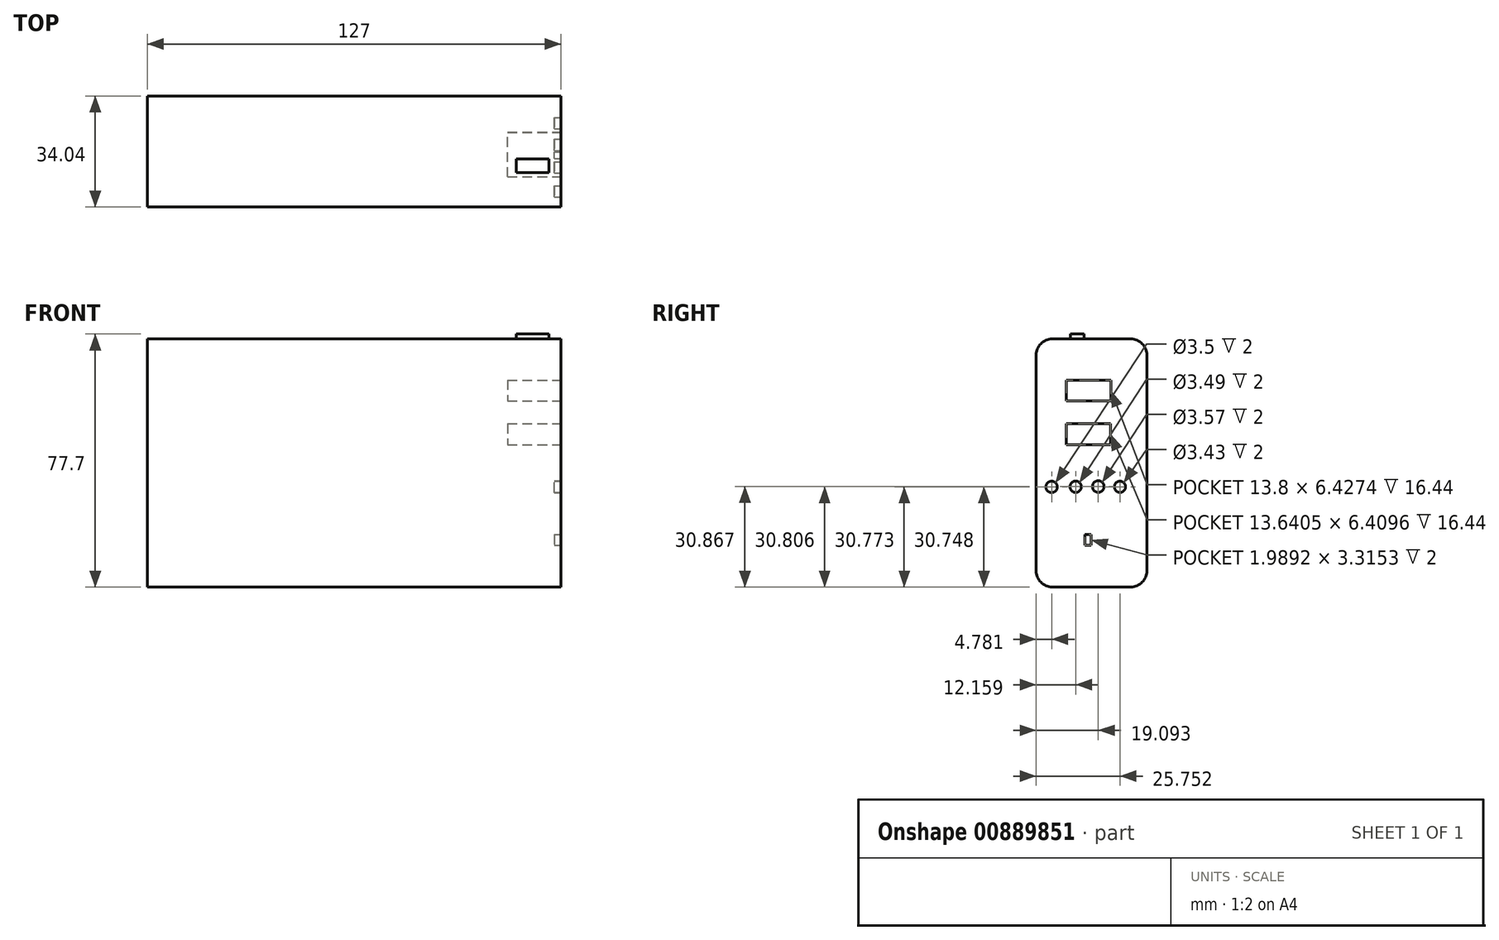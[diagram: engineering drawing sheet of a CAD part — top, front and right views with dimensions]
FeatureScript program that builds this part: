
annotation { "Feature Type Name" : "Feature", "Feature Type Description" : "" }
export const myFeature = defineFeature(function(context is Context, id is Id, definition is map)
    precondition{}
    {
        {
            var Q0;
            Q0=qCreatedBy(makeId("Front.planeOp"),FACE);
            var sketch = newSketch(context, id + "F0", { "sketchPlane" : qUnion([Q0])});
            skLineSegment(sketch, "E0.bottom", {"start": v(63.5, -38.1) * mm, "end": v(-63.5, -38.1) * mm});
            skLineSegment(sketch, "E0.top", {"start": v(63.5, 38.1) * mm, "end": v(-63.5, 38.1) * mm});
            skLineSegment(sketch, "E0.left", {"start": v(63.5, -38.1) * mm, "end": v(63.5, 38.1) * mm});
            skLineSegment(sketch, "E0.right", {"start": v(-63.5, -38.1) * mm, "end": v(-63.5, 38.1) * mm});
            skPoint(sketch, "E0.middle", {"position": v(0, 0) * mm});
            skSolve(sketch);
        }
        {
            var Q0;
            Q0=makeQuery(id+"F0.imprint","IMPRINT",FACE,{"disambiguationData":[TD([[makeQuery(id+"F0.imprint","IMPRINT",EDGE,{"derivedFrom":sQuery(id+"F0.wireOp",EDGE,"E0.bottom")}),-1.0]])]});
            extrude(context, id + "F1", {"entities" : qUnion([Q0]), "depth" : 34.04 * mm, "offsetDistance" : 25.4 * mm});
        }
        {
            var Q0;
            Q0=makeQuery(id+"F1.opExtrude","CAP_EDGE",EDGE,{"disambiguationData":[OSD([sQuery(id+"F0.wireOp",EDGE,"E0.top")])],"isStart":false});
            var Q1;
            Q1=makeQuery(id+"F1.opExtrude","CAP_EDGE",EDGE,{"disambiguationData":[OSD([sQuery(id+"F0.wireOp",EDGE,"E0.top")])],"isStart":true});
            var Q2;
            Q2=makeQuery(id+"F1.opExtrude","CAP_EDGE",EDGE,{"disambiguationData":[OSD([sQuery(id+"F0.wireOp",EDGE,"E0.bottom")])],"isStart":false});
            var Q3;
            Q3=makeQuery(id+"F1.opExtrude","CAP_EDGE",EDGE,{"disambiguationData":[OSD([sQuery(id+"F0.wireOp",EDGE,"E0.bottom")])],"isStart":true});
            fillet(context, id + "F2", {"entities" : qUnion([Q0, Q1, Q2, Q3]), "radius" : 5 * mm, "tangentPropagation" : true, "allowEdgeOverflow" : false});
        }
        {
            var Q0;
            Q0=makeQuery(id+"F1.opExtrude","SWEPT_FACE",FACE,{"disambiguationData":[OSD([sQuery(id+"F0.wireOp",EDGE,"E0.left")])]});
            var sketch = newSketch(context, id + "F3", { "sketchPlane" : qUnion([Q0])});
            skLineSegment(sketch, "E1.bottom", {"start": v(-24.8, 25.43) * mm, "end": v(-11, 25.43) * mm});
            skLineSegment(sketch, "E1.top", {"start": v(-24.8, 19) * mm, "end": v(-11, 19) * mm});
            skLineSegment(sketch, "E1.left", {"start": v(-24.8, 25.43) * mm, "end": v(-24.8, 19) * mm});
            skLineSegment(sketch, "E1.right", {"start": v(-11, 25.43) * mm, "end": v(-11, 19) * mm});
            skSolve(sketch);
        }
        {
            var Q0;
            Q0 = qSketchRegion(id + "F3", true);
            extrude(context, id + "F4", {"entities" : qUnion([Q0]), "operationType" : NewBodyOperationType.REMOVE, "oppositeDirection" : true, "depth" : 16.44 * mm, "offsetDistance" : 25.4 * mm});
        }
        {
            var Q0;
            Q0=makeQuery(id+"F1.opExtrude","SWEPT_FACE",FACE,{"disambiguationData":[OSD([sQuery(id+"F0.wireOp",EDGE,"E0.left")])]});
            var sketch = newSketch(context, id + "F5", { "sketchPlane" : qUnion([Q0])});
            skLineSegment(sketch, "E2.bottom", {"start": v(-24.8, 12.05) * mm, "end": v(-11.16, 12.05) * mm});
            skLineSegment(sketch, "E2.top", {"start": v(-24.8, 5.64) * mm, "end": v(-11.16, 5.64) * mm});
            skLineSegment(sketch, "E2.left", {"start": v(-24.8, 12.05) * mm, "end": v(-24.8, 5.64) * mm});
            skLineSegment(sketch, "E2.right", {"start": v(-11.16, 12.05) * mm, "end": v(-11.16, 5.64) * mm});
            skSolve(sketch);
        }
        {
            var Q0;
            Q0 = qSketchRegion(id + "F5", true);
            extrude(context, id + "F6", {"entities" : qUnion([Q0]), "operationType" : NewBodyOperationType.REMOVE, "oppositeDirection" : true, "depth" : 16.44 * mm, "offsetDistance" : 25.4 * mm});
        }
        {
            var Q0;
            Q0=makeQuery(id+"F1.opExtrude","SWEPT_FACE",FACE,{"disambiguationData":[OSD([sQuery(id+"F0.wireOp",EDGE,"E0.left")])]});
            var sketch = newSketch(context, id + "F7", { "sketchPlane" : qUnion([Q0])});
            skCircle(sketch, "E3", {"center": v(-29.26, -7.35) * mm, "radius": 1.75 * mm});
            skPoint(sketch, "E3.first.point", {"position": v(-30.17, -5.86) * mm});
            skPoint(sketch, "E3.second.point", {"position": v(-28.18, -8.73) * mm});
            skPoint(sketch, "E3.third.point", {"position": v(-27.52, -7.18) * mm});
            skSolve(sketch);
        }
        {
            var Q0;
            Q0 = qSketchRegion(id + "F7", true);
            extrude(context, id + "F8", {"entities" : qUnion([Q0]), "operationType" : NewBodyOperationType.REMOVE, "oppositeDirection" : true, "depth" : 2 * mm, "offsetDistance" : 25.4 * mm});
        }
        {
            var Q0;
            Q0=makeQuery(id+"F1.opExtrude","SWEPT_FACE",FACE,{"disambiguationData":[OSD([sQuery(id+"F0.wireOp",EDGE,"E0.left")])]});
            var sketch = newSketch(context, id + "F9", { "sketchPlane" : qUnion([Q0])});
            skCircle(sketch, "E4", {"center": v(-21.88, -7.3) * mm, "radius": 1.75 * mm});
            skPoint(sketch, "E4.first.point", {"position": v(-23.32, -6.3) * mm});
            skPoint(sketch, "E4.second.point", {"position": v(-20.22, -7.85) * mm});
            skPoint(sketch, "E4.third.point", {"position": v(-20.44, -8.29) * mm});
            skSolve(sketch);
        }
        {
            var Q0;
            Q0 = qSketchRegion(id + "F9", true);
            extrude(context, id + "F10", {"entities" : qUnion([Q0]), "operationType" : NewBodyOperationType.REMOVE, "oppositeDirection" : true, "depth" : 2 * mm, "offsetDistance" : 25.4 * mm});
        }
        {
            var Q0;
            Q0=makeQuery(id+"F1.opExtrude","SWEPT_FACE",FACE,{"disambiguationData":[OSD([sQuery(id+"F0.wireOp",EDGE,"E0.left")])]});
            var sketch = newSketch(context, id + "F11", { "sketchPlane" : qUnion([Q0])});
            skCircle(sketch, "E5", {"center": v(-14.95, -7.23) * mm, "radius": 1.78 * mm});
            skPoint(sketch, "E5.first.point", {"position": v(-16.47, -6.3) * mm});
            skPoint(sketch, "E5.second.point", {"position": v(-13.37, -8.07) * mm});
            skPoint(sketch, "E5.third.point", {"position": v(-13.81, -5.86) * mm});
            skSolve(sketch);
        }
        {
            var Q0;
            Q0 = qSketchRegion(id + "F11", true);
            extrude(context, id + "F12", {"entities" : qUnion([Q0]), "operationType" : NewBodyOperationType.REMOVE, "oppositeDirection" : true, "depth" : 2 * mm, "offsetDistance" : 25.4 * mm});
        }
        {
            var Q0;
            Q0=makeQuery(id+"F1.opExtrude","SWEPT_FACE",FACE,{"disambiguationData":[OSD([sQuery(id+"F0.wireOp",EDGE,"E0.left")])]});
            var sketch = newSketch(context, id + "F13", { "sketchPlane" : qUnion([Q0])});
            skCircle(sketch, "E6", {"center": v(-8.29, -7.33) * mm, "radius": 1.72 * mm});
            skPoint(sketch, "E6.first.point", {"position": v(-9.17, -5.86) * mm});
            skPoint(sketch, "E6.second.point", {"position": v(-6.74, -8.07) * mm});
            skPoint(sketch, "E6.third.point", {"position": v(-7.4, -5.86) * mm});
            skSolve(sketch);
        }
        {
            var Q0;
            Q0 = qSketchRegion(id + "F13", true);
            extrude(context, id + "F14", {"entities" : qUnion([Q0]), "operationType" : NewBodyOperationType.REMOVE, "oppositeDirection" : true, "depth" : 2 * mm, "offsetDistance" : 25.4 * mm});
        }
        {
            var Q0;
            Q0=makeQuery(id+"F1.opExtrude","SWEPT_FACE",FACE,{"disambiguationData":[OSD([sQuery(id+"F0.wireOp",EDGE,"E0.left")])]});
            var sketch = newSketch(context, id + "F15", { "sketchPlane" : qUnion([Q0])});
            skLineSegment(sketch, "E7.bottom", {"start": v(-19.12, -22) * mm, "end": v(-17.13, -22) * mm});
            skLineSegment(sketch, "E7.top", {"start": v(-19.12, -25.3) * mm, "end": v(-17.13, -25.3) * mm});
            skLineSegment(sketch, "E7.left", {"start": v(-19.12, -22) * mm, "end": v(-19.12, -25.3) * mm});
            skLineSegment(sketch, "E7.right", {"start": v(-17.13, -22) * mm, "end": v(-17.13, -25.3) * mm});
            skSolve(sketch);
        }
        {
            var Q0;
            Q0 = qSketchRegion(id + "F15", true);
            extrude(context, id + "F16", {"entities" : qUnion([Q0]), "operationType" : NewBodyOperationType.REMOVE, "oppositeDirection" : true, "depth" : 2 * mm, "offsetDistance" : 25.4 * mm});
        }
        {
            var Q0;
            Q0=makeQuery(id+"F1.opExtrude","SWEPT_FACE",FACE,{"disambiguationData":[OSD([sQuery(id+"F0.wireOp",EDGE,"E0.top")])]});
            var sketch = newSketch(context, id + "F17", { "sketchPlane" : qUnion([Q0])});
            skLineSegment(sketch, "E8.bottom", {"start": v(49.84, -23.54) * mm, "end": v(59.79, -23.54) * mm});
            skLineSegment(sketch, "E8.top", {"start": v(49.84, -19.34) * mm, "end": v(59.79, -19.34) * mm});
            skLineSegment(sketch, "E8.left", {"start": v(49.84, -23.54) * mm, "end": v(49.84, -19.34) * mm});
            skLineSegment(sketch, "E8.right", {"start": v(59.79, -23.54) * mm, "end": v(59.79, -19.34) * mm});
            skSolve(sketch);
        }
        {
            var Q0;
            Q0 = qSketchRegion(id + "F17", true);
            extrude(context, id + "F18", {"entities" : qUnion([Q0]), "operationType" : NewBodyOperationType.ADD, "depth" : 1.5 * mm, "offsetDistance" : 25.4 * mm});
        }
    });
